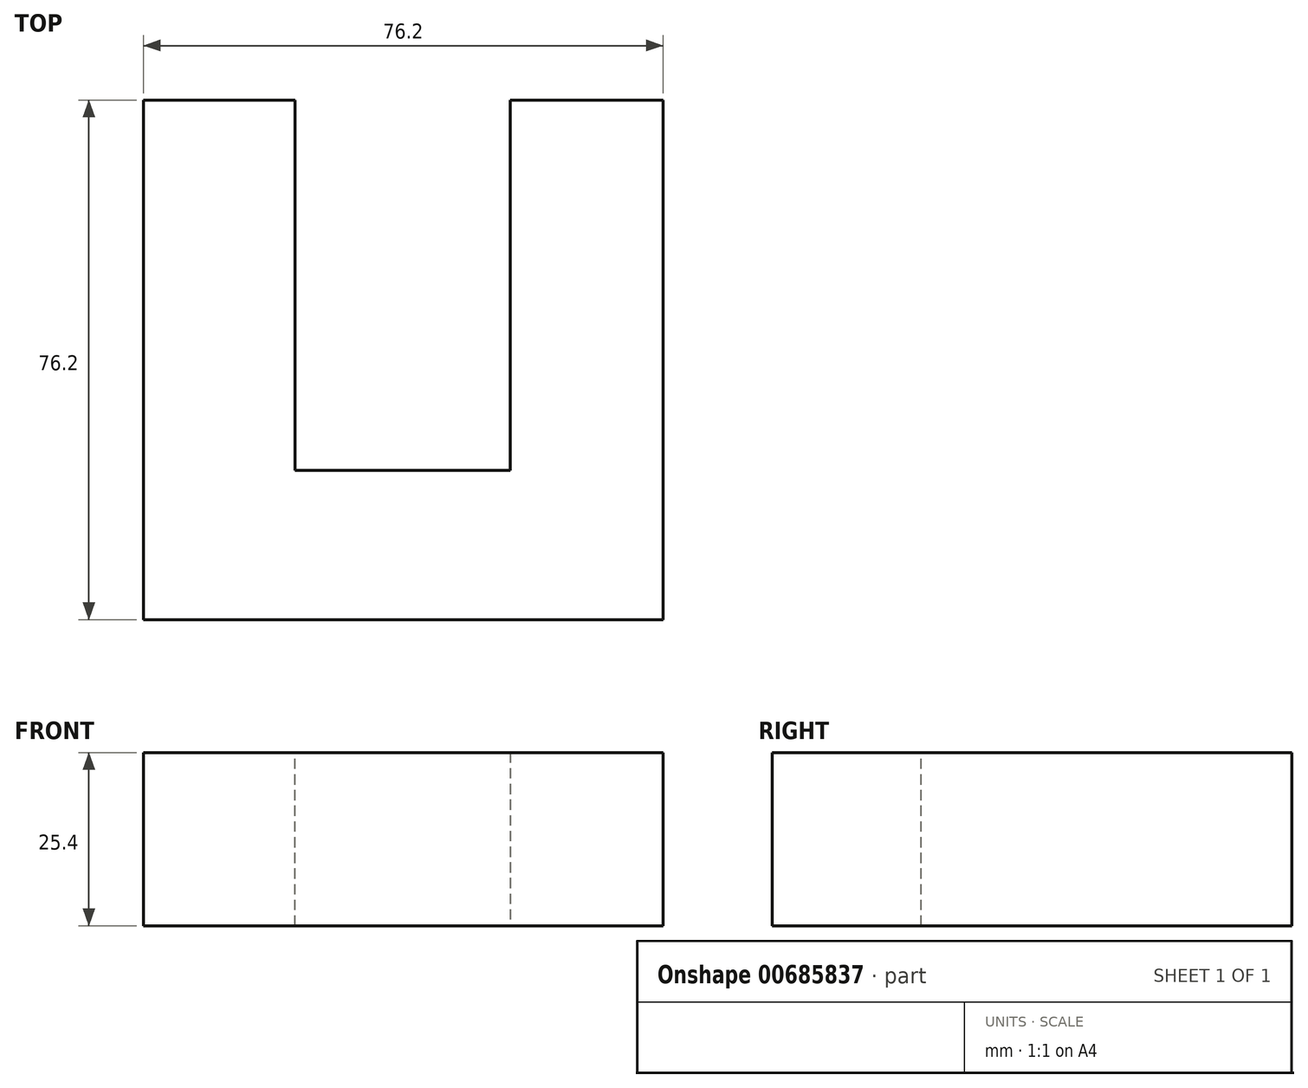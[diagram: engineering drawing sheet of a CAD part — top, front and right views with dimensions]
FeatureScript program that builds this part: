
annotation { "Feature Type Name" : "Feature", "Feature Type Description" : "" }
export const myFeature = defineFeature(function(context is Context, id is Id, definition is map)
    precondition{}
    {
        {
            var Q0;
            Q0=qCreatedBy(makeId("Top.planeOp"),FACE);
            var sketch = newSketch(context, id + "F0", { "sketchPlane" : qUnion([Q0])});
            skLineSegment(sketch, "E0.bottom", {"start": v(-53.76, 43.99) * mm, "end": v(-27.94, 43.99) * mm});
            skLineSegment(sketch, "E0.top", {"start": v(-53.76, -32.21) * mm, "end": v(22.44, -32.21) * mm});
            skLineSegment(sketch, "E0.left", {"start": v(-53.76, 43.99) * mm, "end": v(-53.76, -32.21) * mm});
            skLineSegment(sketch, "E0.right", {"start": v(22.44, 43.99) * mm, "end": v(22.44, -32.21) * mm});
            skLineSegment(sketch, "E1", {"start": v(-27.94, 43.99) * mm, "end": v(-27.94, 5.89) * mm});
            skLineSegment(sketch, "E2", {"start": v(-27.94, 5.89) * mm, "end": v(0, 5.89) * mm});
            skLineSegment(sketch, "E3", {"start": v(0, 5.89) * mm, "end": v(0, 43.99) * mm});
            skLineSegment(sketch, "E4.trimOffspring", {"start": v(0, 43.99) * mm, "end": v(22.44, 43.99) * mm});
            skSolve(sketch);
        }
        {
            var Q0;
            Q0 = qSketchRegion(id + "F0", true);
            extrude(context, id + "F1", {"entities" : qUnion([Q0]), "depth" : 25.4 * mm, "offsetDistance" : 25.4 * mm});
        }
        {
            var Q0;
            Q0=makeQuery(id+"F1.opExtrude","CAP_FACE",FACE,{"disambiguationData":[OSD([sQuery(id+"F0.wireOp",EDGE,"E0.bottom"),sQuery(id+"F0.wireOp",EDGE,"E0.top"),sQuery(id+"F0.wireOp",EDGE,"E0.left"),sQuery(id+"F0.wireOp",EDGE,"E0.right"),sQuery(id+"F0.wireOp",EDGE,"E1"),sQuery(id+"F0.wireOp",EDGE,"E2"),sQuery(id+"F0.wireOp",EDGE,"E3"),sQuery(id+"F0.wireOp",EDGE,"E4.trimOffspring")])],"isStart":false});
            var sketch = newSketch(context, id + "F2", { "sketchPlane" : qUnion([Q0])});
            skLineSegment(sketch, "E5", {"start": v(-31.52, 43.99) * mm, "end": v(-31.52, 0) * mm});
            skLineSegment(sketch, "E6", {"start": v(-31.52, 0) * mm, "end": v(-31.52, -10.35) * mm});
            skLineSegment(sketch, "E7", {"start": v(-31.52, -10.35) * mm, "end": v(0, -10.35) * mm});
            skLineSegment(sketch, "E8", {"start": v(0, -10.35) * mm, "end": v(0, 5.89) * mm});
            skSolve(sketch);
        }
        {
            var Q0;
            Q0 = qSketchRegion(id + "F0Uda7zNDfWB5do_1", true);
            var Q1;
            {var subQ2=sQuery(id+"F2.wireOp",EDGE,"E5");Q1=makeQuery(id+"F2.imprint","IMPRINT",FACE,{"disambiguationData":[TD([[makeQuery(id+"F2.imprint","IMPRINT",EDGE,{"derivedFrom":subQ2}),1.0]])]});}
            extrude(context, id + "F3", {"entities" : qUnion([Q0, Q1]), "operationType" : NewBodyOperationType.REMOVE, "oppositeDirection" : true, "depth" : 25.4 * mm, "offsetDistance" : 25.4 * mm});
        }
    });
